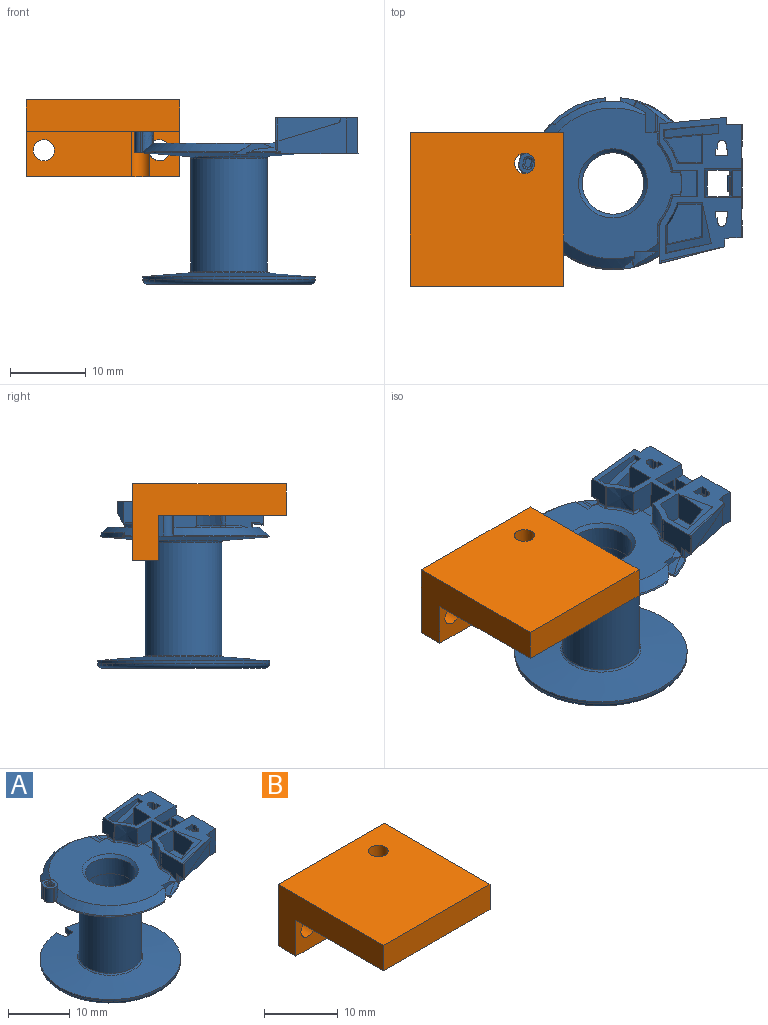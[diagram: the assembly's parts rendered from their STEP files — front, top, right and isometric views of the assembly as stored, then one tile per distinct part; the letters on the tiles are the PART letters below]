
ASSEMBLY  parts=2 mates=1
PART A: 227 faces, bbox 29.8x26x26.2 mm
  f0: plane 4.7x1.43mm, normal (0,1,-0.09), area 3.6mm2, adj f3,f7,f8,f9,f126,f138,f141,f142
  f1: plane 4.7x2.08mm, normal (0,-1,-0.09), area 7.1mm2, adj f3,f5,f8,f119,f125,f131,f134,f135
  f2: plane 1.66x1.65mm, normal (1,0,-0.02), area 1.7mm2, adj f3,f6,f106,f107,f173
  f3: plane 19.25x10.74mm, normal (0,0,1), area 80.5mm2, adj f0,f1,f2,f9,f14,f16,f24,f26
  f4: plane 1.77x0.99mm, normal (0,0,-1), area 1.7mm2, adj f108,f109,f120,f125
  f5: plane 1.77x0.99mm, normal (0,0,-1), area 1.7mm2, adj f1,f107,f119,f125
  f6: plane 2.9x2.58mm, normal (0,0,-1), area 4.7mm2, adj f2,f33,f106,f114,f126,f173
  f7: plane 2.9x2.58mm, normal (0,0,-1), area 4.7mm2, adj f0,f9,f33,f112,f126,f172
  f8: plane 15.75x10.87mm, normal (0,0,-1), area 69.6mm2, adj f0,f1,f56,f57,f78,f79,f106,f108
  f9: plane 1.66x1.65mm, normal (1,0,-0.02), area 1.7mm2, adj f0,f3,f7,f109,f172
  f10: cylinder r=0.42mm len=2mm, axis (0,-1,0), area 2.5mm2, adj f11,f12,f22,f23,f33,f110
  f11: plane 0.52x0.43mm, normal (0,-1,0.05), area 0.2mm2, adj f10,f22,f110,f111,f123
  f12: plane 0.52x0.43mm, normal (0,1,0.05), area 0.2mm2, adj f10,f23,f110,f113,f123
  f13: plane 7.19x1.77mm, normal (-0.17,-0.02,0.98), area 7.7mm2, adj f14,f18,f24,f26,f117,f118
  f14: plane 7.29x1.92mm, normal (0.1,-0.99,0.05), area 9.4mm2, adj f3,f13,f24,f118
  f15: plane 6.57x1.31mm, normal (0,0,-1), area 8.6mm2, adj f107,f109,f125,f207
  f16: plane 3.7x3.33mm, normal (0,1,0), area 11.3mm2, adj f3,f38,f116,f127,f128,f222
  f17: plane 2.8x0.3mm, normal (-0.23,-0.97,0.02), area 0.8mm2, adj f32,f79,f168,f177
  f18: plane 4.99x2.65mm, normal (0.1,-0.99,0.05), area 10.8mm2, adj f13,f24,f25,f26
  f19: plane 4.77x3.42mm, normal (-0.21,0.98,0.05), area 12.9mm2, adj f27,f28,f29,f41
  f20: cone r=8.77mm half-angle=72.8deg, axis (-0.02,0,-1), area 1.4mm2, adj f30,f31,f44,f219
  f21: plane 2.7x0.65mm, normal (-0.97,0.23,0.02), area 1.7mm2, adj f32,f79,f165,f177
  f22: plane 0.44x0.43mm, normal (0,-1,-0.05), area 0.1mm2, adj f10,f11,f33
  f23: plane 0.44x0.42mm, normal (0,1,-0.05), area 0.1mm2, adj f10,f12,f33
  f24: plane 3.7x1.25mm, normal (1,0,0.05), area 2.4mm2, adj f3,f13,f14,f18,f34
  f25: plane 4.76x3.61mm, normal (0,0,1), area 12.9mm2, adj f18,f26,f34,f35
  f26: plane 3.96x3.7mm, normal (-1,0,0.05), area 14mm2, adj f3,f13,f18,f25,f35,f117
  f27: plane 6.4x5.92mm, normal (-0.27,-0.06,0.96), area 8.3mm2, adj f3,f19,f28,f41,f42
  f28: plane 4.57x3.7mm, normal (-1,0,0.05), area 15.7mm2, adj f3,f19,f27,f29,f43
  f29: plane 5.22x4.48mm, normal (0,0,1), area 18.8mm2, adj f19,f28,f40,f41,f43
  f30: plane 8.28x2.85mm, normal (0.27,0.06,-0.96), area 8.8mm2, adj f20,f44,f57,f218
  f31: plane 8.22x3.05mm, normal (0.25,-0.97,0), area 15.5mm2, adj f20,f37,f44,f45,f219
  f32: plane 2.74x2.47mm, normal (0,0,1), area 3.3mm2, adj f17,f21,f46,f47,f165,f168,f170,f177
  f33: plane 7.19x3.31mm, normal (-1,0,-0.09), area 11.2mm2, adj f6,f7,f10,f22,f23,f107,f109,f111
  f34: cone r=8.86mm half-angle=3deg, axis (0,0,-1), area 13.7mm2, adj f3,f24,f25,f35
  f35: plane 3.7x3.33mm, normal (0,1,0.05), area 11.7mm2, adj f3,f25,f26,f34
  f36: plane 3.05x2.54mm, normal (-1,0,0.02), area 7.3mm2, adj f3,f49,f209,f210,f212,f213
  f37: cone r=8.87mm half-angle=88.9deg, axis (-0.02,0,-1), area 1.4mm2, adj f3,f31,f44
  f38: cylinder r=8.05mm len=3.2mm, axis (0,0,-1), area 10.8mm2, adj f3,f16,f164,f224
  f39: cone r=8.11mm half-angle=1deg, axis (0,0,1), area 11.7mm2, adj f3,f115,f213,f215,f216
  f40: cone r=8.86mm half-angle=3deg, axis (0,0,-1), area 12.1mm2, adj f3,f29,f41,f43
  f41: plane 3.73x3.7mm, normal (1,0,0.05), area 11.2mm2, adj f3,f19,f27,f29,f40,f42
  f42: plane 6.01x1.75mm, normal (-0.21,0.98,0.05), area 5.4mm2, adj f3,f27,f41
  f43: plane 3.7x3.33mm, normal (0,-1,0.05), area 11.7mm2, adj f3,f28,f29,f40
  f44: plane 1.06x0.6mm, normal (0.99,-0.1,-0.02), area 0.6mm2, adj f3,f20,f30,f31,f37,f57
  f45: plane 3.09x0.32mm, normal (0.25,-0.97,0), area 0.8mm2, adj f3,f31,f50,f219
  f46: plane 2.8x0.3mm, normal (0.23,0.97,0.02), area 0.8mm2, adj f32,f79,f165,f170
  f47: plane 1.85x0.66mm, normal (0.97,-0.23,0.02), area 1.2mm2, adj f32,f63,f168,f170
  f48: plane 1.29x0.04mm, normal (0,1,0), area 0.1mm2, adj f3,f49,f53,f163
  f49: plane 8.78x3mm, normal (-0.1,1,0), area 19.8mm2, adj f3,f36,f48,f54,f163,f209
  f50: plane 5.12x4.09mm, normal (-1,0,0.02), area 15.5mm2, adj f3,f45,f60,f164,f217,f218,f219,f221
  f51: plane 2.55x0.17mm, normal (1,0,0), area 0.4mm2, adj f52,f63,f78,f198
  f52: plane 19.97x19.06mm, normal (0,0,1), area 213.7mm2, adj f51,f60,f61,f63,f70,f78,f127,f176
  f53: plane 1.1x1mm, normal (1,0.05,0), area 1.1mm2, adj f3,f48,f78,f163
  f54: plane 8.2x1.79mm, normal (0.17,0.02,-0.98), area 8.3mm2, adj f49,f78,f163,f209
  f55: cone r=11.26mm half-angle=50deg, axis (0,0,-1), area 3.6mm2, adj f64,f65,f66,f67,f78,f226
  f56: cylinder r=397.74mm len=5.46mm, axis (-1,0,0), area 3.3mm2, adj f8,f57,f79
  f57: plane 9.37x4.7mm, normal (0.22,-0.98,0), area 28.7mm2, adj f3,f8,f30,f44,f56,f60,f68,f79
  f58: cylinder r=6.87mm len=2.85mm, axis (0,1,0), area 3.2mm2, adj f59,f60,f68,f69,f70
  f59: plane 0.58x0.35mm, normal (0,0,1), area 0.1mm2, adj f58,f60,f70
  f60: cone r=11.26mm half-angle=50deg, axis (0,0,-1), area 3.6mm2, adj f50,f52,f57,f58,f59,f68,f70,f217
  f61: plane 0.85x0.25mm, normal (1,0,0), area 0.2mm2, adj f52,f62,f63,f70
  f62: plane 2.37x2.17mm, normal (0.5,0,-0.87), area 3.9mm2, adj f61,f63,f70,f71,f72
  f63: cone r=10.86mm half-angle=50deg, axis (0,0,-1), area 58.2mm2, adj f47,f51,f52,f61,f62,f72,f73,f74
  f64: plane 2.19x2.13mm, normal (0,0,1), area 2.5mm2, adj f55,f78,f226
  f65: plane 4.61x4.48mm, normal (-0.17,0,0.98), area 13.2mm2, adj f55,f66,f78,f226
  f66: bspline ~4.64x2.33mm, area 1.5mm2, adj f55,f65,f67,f78,f79
  f67: revolved ~5.8x3.88mm, area 1.5mm2, adj f55,f66,f78,f79
  f68: revolved ~4.15x2.03mm, area 1mm2, adj f57,f58,f60,f69,f79
  f69: bspline ~2.16x0.86mm, area 0.6mm2, adj f58,f68,f70,f79
  f70: plane 5.28x1.57mm, normal (0,-1,0), area 3mm2, adj f52,f58,f59,f60,f61,f62,f69,f71
  f71: bspline ~2.35x0.37mm, area 0.1mm2, adj f62,f70,f72,f79
  f72: revolved ~12.66x12.65mm, area 4.4mm2, adj f62,f63,f71,f79,f168
  f73: revolved ~4.1x2.68mm, area 1.1mm2, adj f63,f74,f79,f170
  f74: plane 0.34x0.18mm, normal (0.71,0.71,0.02), area 0.1mm2, adj f63,f73,f75,f79
  f75: bspline ~0.57x0.35mm, area 0.2mm2, adj f63,f74,f76,f79
  f76: cone r=10.87mm half-angle=1deg, axis (0,0,-1), area 4.5mm2, adj f63,f75,f77,f79
  f77: plane 7.9x5.02mm, normal (0.17,0,-0.98), area 30mm2, adj f63,f76,f78,f79,f198
  f78: plane 19.21x5.04mm, normal (-0.1,1,0), area 27.8mm2, adj f3,f8,f51,f52,f53,f54,f55,f64
  f79: cone r=12.75mm half-angle=85.5deg, axis (0,0,1), area 266.9mm2, adj f8,f17,f21,f46,f56,f57,f66,f67
  f80: plane 0.63x0.51mm, normal (0,0,-1), area 0.3mm2, adj f82,f83,f84,f85
  f81: plane 0.8x0.67mm, normal (0,0,-1), area 0.4mm2, adj f86,f87,f88,f89
  f82: bspline ~0.32x0.25mm, area 0mm2, adj f80,f83,f85,f91
  f83: bspline ~0.32x0.24mm, area 0mm2, adj f80,f82,f84,f91
  f84: bspline ~0.31x0.27mm, area 0mm2, adj f80,f83,f85,f91
  f85: bspline ~0.32x0.26mm, area 0mm2, adj f80,f82,f84,f91
  f86: bspline ~0.41x0.35mm, area 0mm2, adj f81,f87,f89,f91
  f87: bspline ~0.39x0.33mm, area 0mm2, adj f81,f86,f88,f91
  f88: bspline ~0.4x0.34mm, area 0mm2, adj f81,f87,f89,f91
  f89: bspline ~0.4x0.32mm, area 0mm2, adj f81,f86,f88,f91
  f90: cylinder r=5.05mm len=14.84mm, axis (0,0,-1), area 470.8mm2, adj f208,f220
  f91: plane 1.67x1.08mm, normal (0,0,-1), area 0.7mm2, adj f82,f83,f84,f85,f86,f87,f88,f89
  f92: bspline ~0.33x0.23mm, area 0mm2, adj f91,f93,f100,f102
  f93: bspline ~0.42x0.31mm, area 0mm2, adj f91,f92,f94,f102
  f94: bspline ~0.33x0.12mm, area 0mm2, adj f91,f93,f95,f102
  f95: bspline ~0.42x0.17mm, area 0mm2, adj f91,f94,f96,f102
  f96: bspline ~0.54x0.49mm, area 0mm2, adj f91,f95,f97,f102
  f97: bspline ~0.44x0.31mm, area 0mm2, adj f91,f96,f98,f102
  f98: bspline ~0.34x0.23mm, area 0mm2, adj f91,f97,f99,f102
  f99: bspline ~0.47x0.41mm, area 0mm2, adj f91,f98,f100,f102
  f100: bspline ~0.45x0.41mm, area 0mm2, adj f91,f92,f99,f102
  f101: cone r=11.37mm half-angle=85.5deg, axis (0,0,-1), area 315.5mm2, adj f103,f145,f146,f147,f167,f174,f220
  f102: plane 2.25x2.25mm, normal (0,0,-1), area 2.6mm2, adj f92,f93,f94,f95,f96,f97,f98,f99
  f103: cone r=11.35mm half-angle=1deg, axis (0,0,1), area 25mm2, adj f101,f145,f147,f225
  f104: cylinder r=1.12mm len=2.25mm, axis (0,0,-1), area 0.1mm2, adj f102,f105
  f105: plane 21.43x21.39mm, normal (0,0,-1), area 252.1mm2, adj f104,f145,f146,f147,f153,f155,f167,f174
  f106: plane 4.7x1.43mm, normal (0,-1,-0.09), area 3.6mm2, adj f2,f3,f6,f8,f126,f133,f134,f137
  f107: plane 4.71x3.48mm, normal (0,1,-0.09), area 8.1mm2, adj f2,f3,f5,f15,f33,f119,f125,f173
  f108: plane 4.7x2.08mm, normal (0,1,-0.09), area 7.1mm2, adj f3,f4,f8,f120,f125,f140,f141,f144
  f109: plane 4.71x3.48mm, normal (0,-1,-0.09), area 8.1mm2, adj f3,f4,f9,f15,f33,f120,f125,f172
  f110: plane 1.96x0.14mm, normal (0,0,1), area 0.3mm2, adj f10,f11,f12,f123
  f111: plane 0.55x0.1mm, normal (0,0,1), area 0.1mm2, adj f11,f33,f112,f123
  f112: plane 4.95x3.95mm, normal (0,1,0.09), area 9.4mm2, adj f3,f7,f33,f111,f123,f124,f125,f126
  f113: plane 0.55x0.1mm, normal (0,0,1), area 0.1mm2, adj f12,f33,f114,f123
  f114: plane 4.95x3.95mm, normal (0,-1,0.09), area 9.4mm2, adj f3,f6,f33,f113,f123,f124,f125,f126
  f115: plane 3.7x3.32mm, normal (0,-1,0), area 11.2mm2, adj f3,f39,f116,f127,f128,f215
  f116: plane 3.7x3.5mm, normal (-1,0,0.05), area 13mm2, adj f3,f16,f115,f128
  f117: plane 2.2x1.06mm, normal (-0.1,1,0), area 1.9mm2, adj f3,f13,f26,f118
  f118: plane 1.2x0.67mm, normal (-1,0,0), area 0.8mm2, adj f3,f13,f14,f117
  f119: plane 1x0.99mm, normal (-1,0,-0.02), area 0.9mm2, adj f1,f3,f5,f107
  f120: plane 1x0.99mm, normal (-1,0,-0.02), area 0.9mm2, adj f3,f4,f108,f109
  f121: plane 4.7x1.5mm, normal (0,-1,0), area 6.9mm2, adj f3,f8,f57,f125
  f122: plane 4.7x1.5mm, normal (0,1,0), area 6.9mm2, adj f3,f8,f78,f125
  f123: plane 3.5x2.29mm, normal (-1,0,0.09), area 6.7mm2, adj f11,f12,f110,f111,f112,f113,f114,f124
  f124: plane 3.5x1.25mm, normal (0,0,1), area 4.4mm2, adj f112,f114,f123,f125
  f125: plane 14.89x4.7mm, normal (1,0,0.02), area 54.3mm2, adj f1,f3,f4,f5,f8,f15,f107,f108
  f126: plane 9.83x3.04mm, normal (1,0,-0.09), area 21.6mm2, adj f0,f6,f7,f8,f106,f112,f114,f130
  f127: cone r=9.03mm half-angle=3deg, axis (0,0,-1), area 1.5mm2, adj f16,f52,f115,f128,f215,f222
  f128: plane 3.5x2.11mm, normal (0,0,1), area 7mm2, adj f16,f115,f116,f127
  f129: plane 3.95x3.79mm, normal (1,0,0.09), area 13.7mm2, adj f3,f112,f114,f130
  f130: plane 3.1x0.08mm, normal (0,0,1), area 0.2mm2, adj f112,f114,f126,f129
  f131: plane 1.12x0.27mm, normal (-1,0,-0.09), area 0.2mm2, adj f1,f132,f190,f194
  f132: cone r=1.09mm half-angle=5deg, axis (0,0,-1), area 3.6mm2, adj f131,f133,f189,f195
  f133: plane 1.12x0.27mm, normal (1,0,-0.09), area 0.2mm2, adj f106,f132,f188,f196
  f134: plane 1.77x1.16mm, normal (0,0,-1), area 0.5mm2, adj f1,f106,f185,f186,f187,f194,f195,f196
  f135: plane 3.3x0.58mm, normal (-1,0,-0.02), area 1.4mm2, adj f1,f3,f136,f185
  f136: cone r=0.57mm half-angle=1deg, axis (0,0,-1), area 6.3mm2, adj f3,f135,f137,f186
  f137: plane 3.3x0.58mm, normal (1,0,-0.02), area 1.4mm2, adj f3,f106,f136,f187
  f138: plane 1.12x0.27mm, normal (1,0,-0.09), area 0.2mm2, adj f0,f139,f181,f191
  f139: cone r=1.09mm half-angle=5deg, axis (0,0,-1), area 3.6mm2, adj f138,f140,f180,f192
  f140: plane 1.12x0.27mm, normal (-1,0,-0.09), area 0.2mm2, adj f108,f139,f179,f193
  f141: plane 1.77x1.16mm, normal (0,0,-1), area 0.5mm2, adj f0,f108,f179,f180,f181,f182,f183,f184
  f142: plane 3.3x0.58mm, normal (1,0,-0.02), area 1.4mm2, adj f0,f3,f143,f182
  f143: cone r=0.57mm half-angle=1deg, axis (0,0,-1), area 6.3mm2, adj f3,f142,f144,f183
  f144: plane 3.3x0.58mm, normal (-1,0,-0.02), area 1.4mm2, adj f3,f108,f143,f184
  f145: plane 1.8x1.16mm, normal (-1,0.02,-0.05), area 1.8mm2, adj f101,f103,f105,f167,f225
  f146: plane 1.54x1.18mm, normal (0,1,-0.05), area 1.7mm2, adj f101,f105,f167,f174
  f147: plane 1.8x1.16mm, normal (1,0.02,-0.05), area 1.8mm2, adj f101,f103,f105,f174,f225
  f148: cone r=11.88mm half-angle=85.5deg, axis (0,0,1), area 0.7mm2, adj f149,f150,f151,f152,f166,f169,f171,f175
  f149: plane 1.52x0.65mm, normal (0.97,-0.23,0.02), area 1mm2, adj f148,f171,f175,f201
  f150: plane 1.55x0.29mm, normal (0.23,0.97,0.02), area 0.4mm2, adj f148,f169,f175,f205
  f151: plane 1.58x0.65mm, normal (-0.97,0.23,0.02), area 1mm2, adj f148,f166,f169,f204
  f152: plane 1.55x0.29mm, normal (-0.23,-0.97,0.02), area 0.4mm2, adj f148,f166,f171,f200
  f153: cylinder r=1.12mm len=2.25mm, axis (0,0,-1), area 0.1mm2, adj f105,f154
  f154: plane 2.25x2.25mm, normal (0,0,-1), area 4mm2, adj f153
  f155: cylinder r=1.12mm len=2.25mm, axis (0,0,-1), area 0.1mm2, adj f105,f156
  f156: plane 2.25x2.25mm, normal (0,0,-1), area 4mm2, adj f155
  f157: cylinder r=4.05mm len=8.1mm, axis (0,0,-1), area 78.9mm2, adj f162,f176
  f158: revolved ~10.72x10.72mm, area 13mm2, adj f159,f178
  f159: plane 10.22x10.22mm, normal (0,0,-1), area 15.5mm2, adj f158,f197
  f160: cone r=4.5mm half-angle=1deg, axis (0,0,-1), area 2.9mm2, adj f161,f197
  f161: plane 9x9mm, normal (0,0,-1), area 8.8mm2, adj f160,f162
  f162: cone r=4.18mm half-angle=0.5deg, axis (0,0,-1), area 373.4mm2, adj f157,f161
  f163: cylinder r=0.45mm len=1.03mm, axis (-0.05,1,0.01), area 0.6mm2, adj f48,f49,f53,f54,f78
  f164: bspline ~3.09x0.68mm, area 2mm2, adj f3,f38,f50,f223
  f165: bspline ~3.94x1.28mm, area 4.4mm2, adj f21,f32,f46,f79
  f166: bspline ~2.2x0.31mm, area 0.6mm2, adj f148,f151,f152,f202
  f167: bspline ~1.42x0.27mm, area 0.4mm2, adj f101,f105,f145,f146
  f168: bspline ~3.99x1.29mm, area 3.5mm2, adj f17,f32,f47,f63,f72,f79
  f169: bspline ~2.2x0.31mm, area 0.6mm2, adj f148,f150,f151,f206
  f170: bspline ~2.81x1.28mm, area 3.5mm2, adj f32,f46,f47,f63,f73,f79
  f171: bspline ~1.53x0.3mm, area 0.6mm2, adj f148,f149,f152,f199
  f172: plane 1.68x0.59mm, normal (0,-0.64,-0.77), area 1.3mm2, adj f7,f9,f33,f109
  f173: plane 1.68x0.59mm, normal (0,0.64,-0.77), area 1.3mm2, adj f2,f6,f33,f107
  f174: bspline ~1.42x0.27mm, area 0.4mm2, adj f101,f105,f146,f147
  f175: bspline ~2.15x0.31mm, area 0.6mm2, adj f148,f149,f150,f203
  f176: cone r=4.55mm half-angle=45deg, axis (0,0,1), area 19.1mm2, adj f52,f157
  f177: bspline ~3.94x1.3mm, area 4.4mm2, adj f17,f21,f32,f79
  f178: torus R=5.46mm, axis (0,0,-1), area 5.3mm2, adj f105,f158
  f179: cylinder r=0.1mm len=0.28mm, axis (0,1,0), area 0mm2, adj f108,f140,f141,f180
  f180: torus R=0.88mm, axis (0,0,-1), area 0.4mm2, adj f139,f141,f179,f181
  f181: cylinder r=0.1mm len=0.28mm, axis (0,-1,0), area 0mm2, adj f0,f138,f141,f180
  f182: cylinder r=0.1mm len=0.29mm, axis (0,1,0), area 0mm2, adj f0,f141,f142,f183
  f183: torus R=0.73mm, axis (0,0,-1), area 0.3mm2, adj f141,f143,f182,f184
  f184: cylinder r=0.1mm len=0.29mm, axis (0,-1,0), area 0mm2, adj f108,f141,f144,f183
  f185: cylinder r=0.1mm len=0.29mm, axis (0,-1,0), area 0mm2, adj f1,f134,f135,f186
  f186: torus R=0.73mm, axis (0,0,-1), area 0.3mm2, adj f134,f136,f185,f187
  f187: cylinder r=0.1mm len=0.29mm, axis (0,1,0), area 0mm2, adj f106,f134,f137,f186
  f188: cylinder r=0.1mm len=0.17mm, axis (0,1,0), area 0mm2, adj f8,f106,f133,f189
  f189: torus R=1.18mm, axis (0,0,-1), area 0.5mm2, adj f8,f132,f188,f190
  f190: cylinder r=0.1mm len=0.17mm, axis (0,-1,0), area 0mm2, adj f1,f8,f131,f189
  f191: cylinder r=0.1mm len=0.17mm, axis (0,1,0), area 0mm2, adj f0,f8,f138,f192
  f192: torus R=1.18mm, axis (0,0,-1), area 0.5mm2, adj f8,f139,f191,f193
  f193: cylinder r=0.1mm len=0.17mm, axis (0,-1,0), area 0mm2, adj f8,f108,f140,f192
  f194: cylinder r=0.1mm len=0.28mm, axis (0,1,0), area 0mm2, adj f1,f131,f134,f195
  f195: torus R=0.88mm, axis (0,0,-1), area 0.4mm2, adj f132,f134,f194,f196
  f196: cylinder r=0.1mm len=0.28mm, axis (0,-1,0), area 0mm2, adj f106,f133,f134,f195
  f197: torus R=4.6mm, axis (0,0,1), area 4.4mm2, adj f159,f160
  f198: cylinder r=0.1mm len=2.72mm, axis (0,1,0), area 0.4mm2, adj f51,f63,f77,f78
  f199: bspline ~0.68x0.46mm, area 0.2mm2, adj f32,f171,f200,f201
  f200: cylinder r=0.25mm len=0.33mm, axis (0.97,-0.23,0), area 0.1mm2, adj f32,f152,f199,f202
  f201: cylinder r=0.25mm len=0.69mm, axis (0.23,0.97,0), area 0.3mm2, adj f32,f149,f199,f203
  f202: bspline ~0.68x0.46mm, area 0.2mm2, adj f32,f166,f200,f204
  f203: bspline ~0.68x0.46mm, area 0.2mm2, adj f32,f175,f201,f205
  f204: cylinder r=0.25mm len=0.69mm, axis (-0.23,-0.97,0), area 0.3mm2, adj f32,f151,f202,f206
  f205: cylinder r=0.25mm len=0.33mm, axis (-0.97,0.23,0), area 0.1mm2, adj f32,f150,f203,f206
  f206: bspline ~0.68x0.46mm, area 0.2mm2, adj f32,f169,f204,f205
  f207: cylinder r=0.25mm len=6.61mm, axis (0,-1,0), area 2.4mm2, adj f15,f33,f107,f109
  f208: torus R=5.3mm, axis (0,0,1), area 12mm2, adj f79,f90
  f209: cylinder r=0.25mm len=1.26mm, axis (0,-1,-0.02), area 0.5mm2, adj f36,f49,f54,f78,f210
  f210: cylinder r=0.25mm len=0.31mm, axis (0.02,0,1), area 0.1mm2, adj f36,f78,f209,f211
  f211: bspline ~0.94x0.52mm, area 0.3mm2, adj f52,f78,f210,f212
  f212: cylinder r=0.25mm len=1.31mm, axis (0,-1,0), area 0.5mm2, adj f36,f52,f211,f214
  f213: bspline ~11.67x0.26mm, area 0.5mm2, adj f3,f36,f39,f214
  f214: bspline ~0.5x0.35mm, area 0.1mm2, adj f52,f212,f213,f216
  f215: cylinder r=0.25mm len=1.24mm, axis (-1,0,0), area 0.4mm2, adj f39,f52,f115,f127,f216
  f216: torus R=7.8mm, axis (0,0,1), area 1.5mm2, adj f39,f52,f214,f215
  f217: cylinder r=0.25mm len=1.65mm, axis (0.02,0,1), area 0.6mm2, adj f50,f57,f60,f218
  f218: cylinder r=0.25mm len=1.3mm, axis (0,-1,-0.06), area 0.5mm2, adj f30,f50,f57,f217,f219
  f219: bspline ~4.5x0.7mm, area 0.2mm2, adj f20,f31,f45,f50,f218
  f220: torus R=5.3mm, axis (0,0,1), area 12mm2, adj f90,f101
  f221: cylinder r=0.25mm len=2.44mm, axis (0,1,0), area 0.8mm2, adj f50,f52,f60,f223
  f222: cylinder r=0.25mm len=1.25mm, axis (1,0,0), area 0.4mm2, adj f16,f52,f127,f224
  f223: bspline ~1.1x0.5mm, area 0.3mm2, adj f52,f164,f221,f224
  f224: torus R=7.8mm, axis (0,0,1), area 1.4mm2, adj f38,f52,f222,f223
  f225: torus R=10.71mm, axis (0,0,-1), area 68.5mm2, adj f103,f105,f145,f147
  f226: cylinder r=2mm len=2.42mm, axis (0,1,0), area 0.8mm2, adj f55,f64,f65,f78
PART B: 12 faces, bbox 20.3x20.3x10.2 mm
  f0: plane 13.93x5.97mm, normal (0,-1,0), area 77mm2, adj f2,f3,f4,f9,f11
  f1: plane 20.28x20.26mm, normal (0,0,1), area 405.3mm2, adj f2,f6,f8,f10,f11
  f2: plane 20.26x10.16mm, normal (-1,0,0), area 105.4mm2, adj f0,f1,f3,f8,f9,f10
  f3: plane 20.28x3.43mm, normal (0,0,-1), area 68.4mm2, adj f0,f2,f6,f7,f8,f11
  f4: cylinder r=1.4mm len=3.43mm, axis (0,1,0), area 30.1mm2, adj f0,f8
  f5: cylinder r=1.4mm len=3.43mm, axis (0,1,0), area 30mm2, adj f7,f8,f11
  f6: plane 20.26x10.16mm, normal (1,0,0), area 105.4mm2, adj f1,f3,f7,f8,f9,f10
  f7: plane 5.97x4mm, normal (0,-1,0), area 17.8mm2, adj f3,f5,f6,f9,f11
  f8: plane 20.28x10.16mm, normal (0,1,0), area 193.8mm2, adj f1,f2,f3,f4,f5,f6
  f9: plane 20.28x16.83mm, normal (0,0,-1), area 336.9mm2, adj f0,f2,f6,f7,f10,f11
  f10: plane 20.28x4.19mm, normal (0,-1,0), area 85mm2, adj f1,f2,f6,f9
  f11: cylinder r=1.33mm len=10.16mm, axis (0,0,-1), area 52.1mm2, adj f0,f1,f3,f5,f7,f9
PLACE A t=(34.44,-5.03,-31.93)mm
PLACE B t=(7.7,1.67,-17.8)mm
MATE planar A.f32 <-> B.f9  axis (0,0,1) through (23.25,-2.34,-11.83)mm
